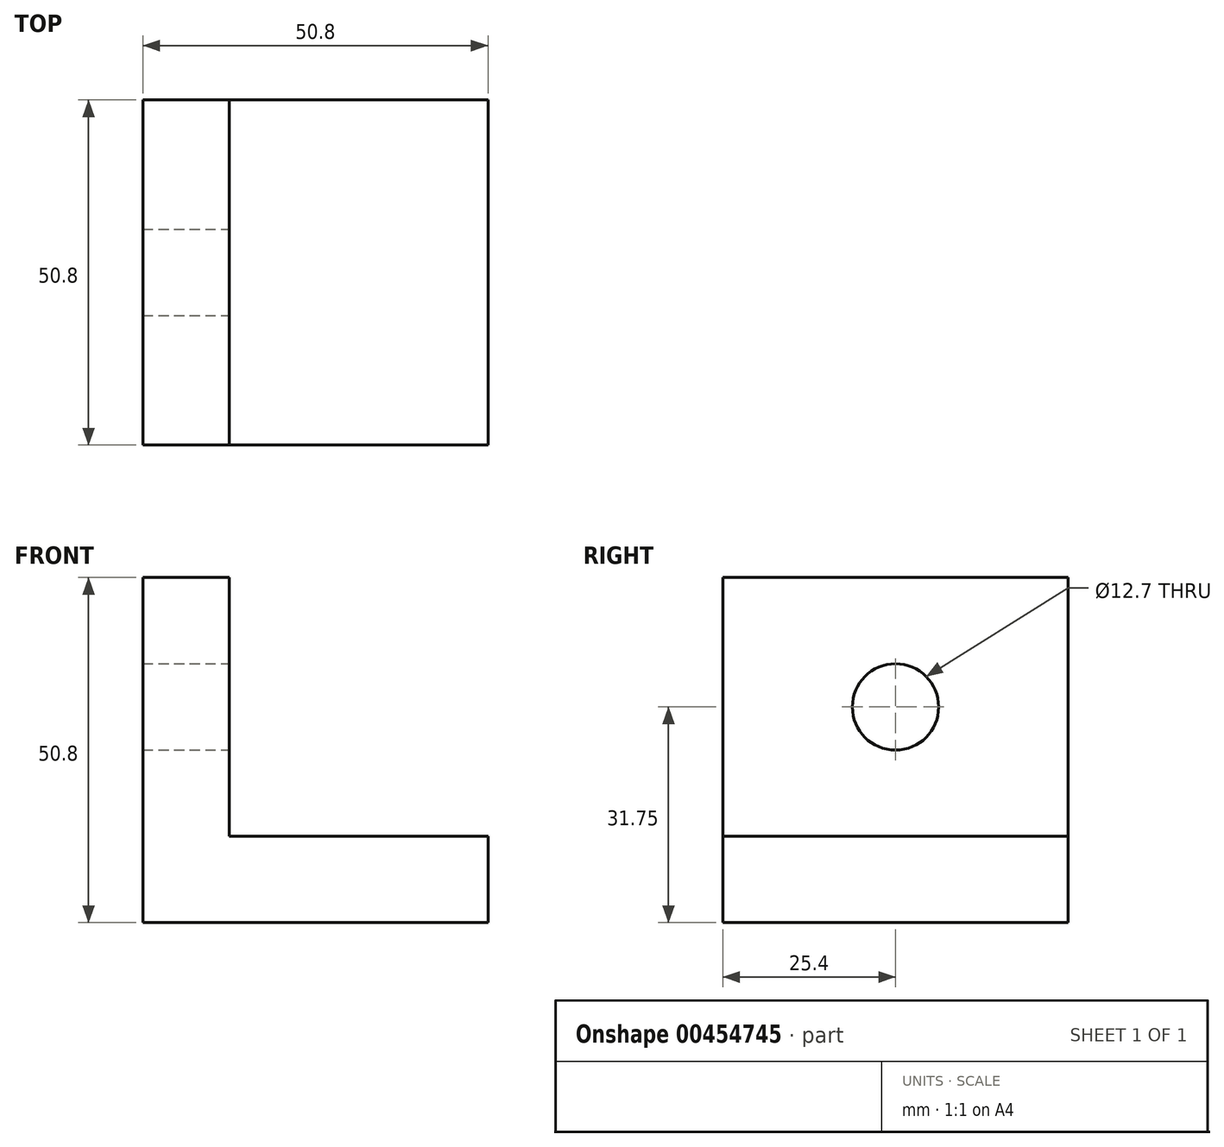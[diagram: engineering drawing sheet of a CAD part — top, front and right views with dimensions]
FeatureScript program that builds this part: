
annotation { "Feature Type Name" : "Feature", "Feature Type Description" : "" }
export const myFeature = defineFeature(function(context is Context, id is Id, definition is map)
    precondition{}
    {
        {
            var Q0;
            Q0=qCreatedBy(makeId("Front.planeOp"),FACE);
            var sketch = newSketch(context, id + "F0", { "sketchPlane" : qUnion([Q0])});
            skLineSegment(sketch, "E0", {"start": v(0, 0) * mm, "end": v(0, 50.8) * mm});
            skLineSegment(sketch, "E1", {"start": v(0, 50.8) * mm, "end": v(12.7, 50.8) * mm});
            skLineSegment(sketch, "E2", {"start": v(12.7, 50.8) * mm, "end": v(12.7, 12.7) * mm});
            skLineSegment(sketch, "E3", {"start": v(12.7, 12.7) * mm, "end": v(50.8, 12.7) * mm});
            skLineSegment(sketch, "E4", {"start": v(50.8, 12.7) * mm, "end": v(50.8, 0) * mm});
            skLineSegment(sketch, "E5", {"start": v(50.8, 0) * mm, "end": v(0, 0) * mm});
            skSolve(sketch);
        }
        {
            var Q0;
            Q0=makeQuery(id+"F0.imprint","IMPRINT",FACE,{"disambiguationData":[TD([[makeQuery(id+"F0.imprint","IMPRINT",EDGE,{"derivedFrom":sQuery(id+"F0.wireOp",EDGE,"E0")}),-1.0]])]});
            extrude(context, id + "F1", {"entities" : qUnion([Q0]), "depth" : 50.8 * mm});
        }
        {
            var Q0;
            Q0=makeQuery(id+"F1.opExtrude","SWEPT_FACE",FACE,{"disambiguationData":[OSD([sQuery(id+"F0.wireOp",EDGE,"E2")])]});
            var sketch = newSketch(context, id + "F2", { "sketchPlane" : qUnion([Q0])});
            skLineSegment(sketch, "E6", {"start": v(-25.4, 50.8) * mm, "end": v(-25.4, 31.75) * mm, "construction": true});
            skPoint(sketch, "E6.endSnap0", {"position": v(-25.4, 12.7) * mm});
            skLineSegment(sketch, "E7", {"start": v(-25.4, 31.75) * mm, "end": v(0, 31.75) * mm, "construction": true});
            skCircle(sketch, "E8", {"center": v(-25.4, 31.75) * mm, "radius": 6.35 * mm});
            skSolve(sketch);
        }
        {
            var Q0;
            Q0=makeQuery(id+"F2.imprint","IMPRINT",FACE,{"disambiguationData":[TD([[makeQuery(id+"F2.imprint","IMPRINT",EDGE,{"derivedFrom":sQuery(id+"F2.wireOp",EDGE,"E8")}),1.0]])]});
            extrude(context, id + "F3", {"entities" : qUnion([Q0]), "operationType" : NewBodyOperationType.REMOVE, "oppositeDirection" : true, "depth" : 25.4 * mm});
        }
    });
